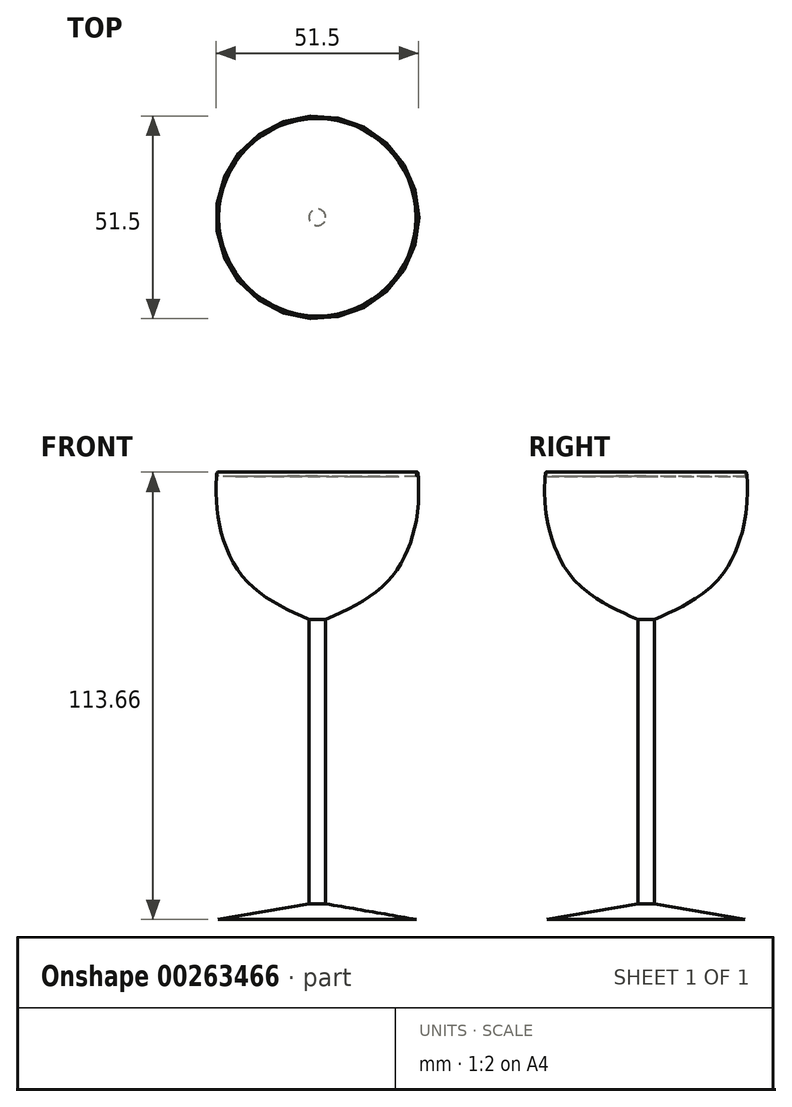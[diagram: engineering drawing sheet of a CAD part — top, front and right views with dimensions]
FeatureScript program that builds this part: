
annotation { "Feature Type Name" : "Feature", "Feature Type Description" : "" }
export const myFeature = defineFeature(function(context is Context, id is Id, definition is map)
    precondition{}
    {
        {
            var Q0;
            Q0=qCreatedBy(makeId("Front.planeOp"),FACE);
            var sketch = newSketch(context, id + "F0", { "sketchPlane" : qUnion([Q0])});
            skLineSegment(sketch, "E0", {"start": v(0, -76.24) * mm, "end": v(-25.18, -76.24) * mm});
            skLineSegment(sketch, "E1", {"start": v(-25.18, -76.24) * mm, "end": v(-2.12, -72.24) * mm});
            skLineSegment(sketch, "E2", {"start": v(-2.12, -72.24) * mm, "end": v(-2.12, 0) * mm});
            skFitSpline(sketch, "E3", {"points": [v(-2.12, 0) * mm, v(-12, 4.94) * mm, v(-19.3, 11.3) * mm, v(-23.53, 19.3) * mm, v(-25.65, 29.65) * mm, v(-25.41, 37.42) * mm, v(-24, 28.24) * mm, v(-21.18, 17.18) * mm, v(-16.24, 10.35) * mm, v(-10.35, 6.12) * mm, v(-4.7, 3.3) * mm, v(0, 2.82) * mm], "startDerivative": vector(-99.39, 44.25) * mm, "endDerivative": vector(69.02, -0.28) * mm});
            skLineSegment(sketch, "E4", {"start": v(0, 2.82) * mm, "end": v(0, -76.24) * mm});
            skLineSegment(sketch, "E5", {"start": v(-25.65, 36.27) * mm, "end": v(0, 36.27) * mm});
            skLineSegment(sketch, "E6", {"start": v(0, 36.27) * mm, "end": v(0, 2.82) * mm});
            skSolve(sketch);
        }
        {
            var Q0;
            Q0 = qSketchRegion(id + "F0", true);
            var Q1;
            Q1=sQuery(id+"F0.wireOp",EDGE,"E4");
            revolve(context, id + "F1", {"entities" : qUnion([Q0]), "axis" : qUnion([Q1]), "revolveType" : RevolveType.FULL});
        }
        {
            var Q0;
            Q0=qCreatedBy(makeId("Front.planeOp"),FACE);
            var sketch = newSketch(context, id + "F2", { "sketchPlane" : qUnion([Q0])});
            skLineSegment(sketch, "E7", {"start": v(0, 0) * mm, "end": v(0, 36.46) * mm});
            skLineSegment(sketch, "E8", {"start": v(0, 36.46) * mm, "end": v(-25.42, 36.23) * mm});
            skFitSpline(sketch, "E9", {"points": [v(-25.42, 36.23) * mm, v(-23.54, 26.34) * mm, v(-17.65, 14.1) * mm, v(-9.42, 7.75) * mm, v(0, 0) * mm], "startDerivative": vector(5.54, -40.26) * mm, "endDerivative": vector(36.5, -32.37) * mm});
            skSolve(sketch);
        }
        {
            var Q0;
            Q0 = qSketchRegion(id + "F2", true);
            var Q1;
            Q1=sQuery(id+"F2.wireOp",EDGE,"E7");
            revolve(context, id + "F3", {"operationType" : NewBodyOperationType.ADD, "entities" : qUnion([Q0]), "axis" : qUnion([Q1]), "revolveType" : RevolveType.FULL});
        }
    });
